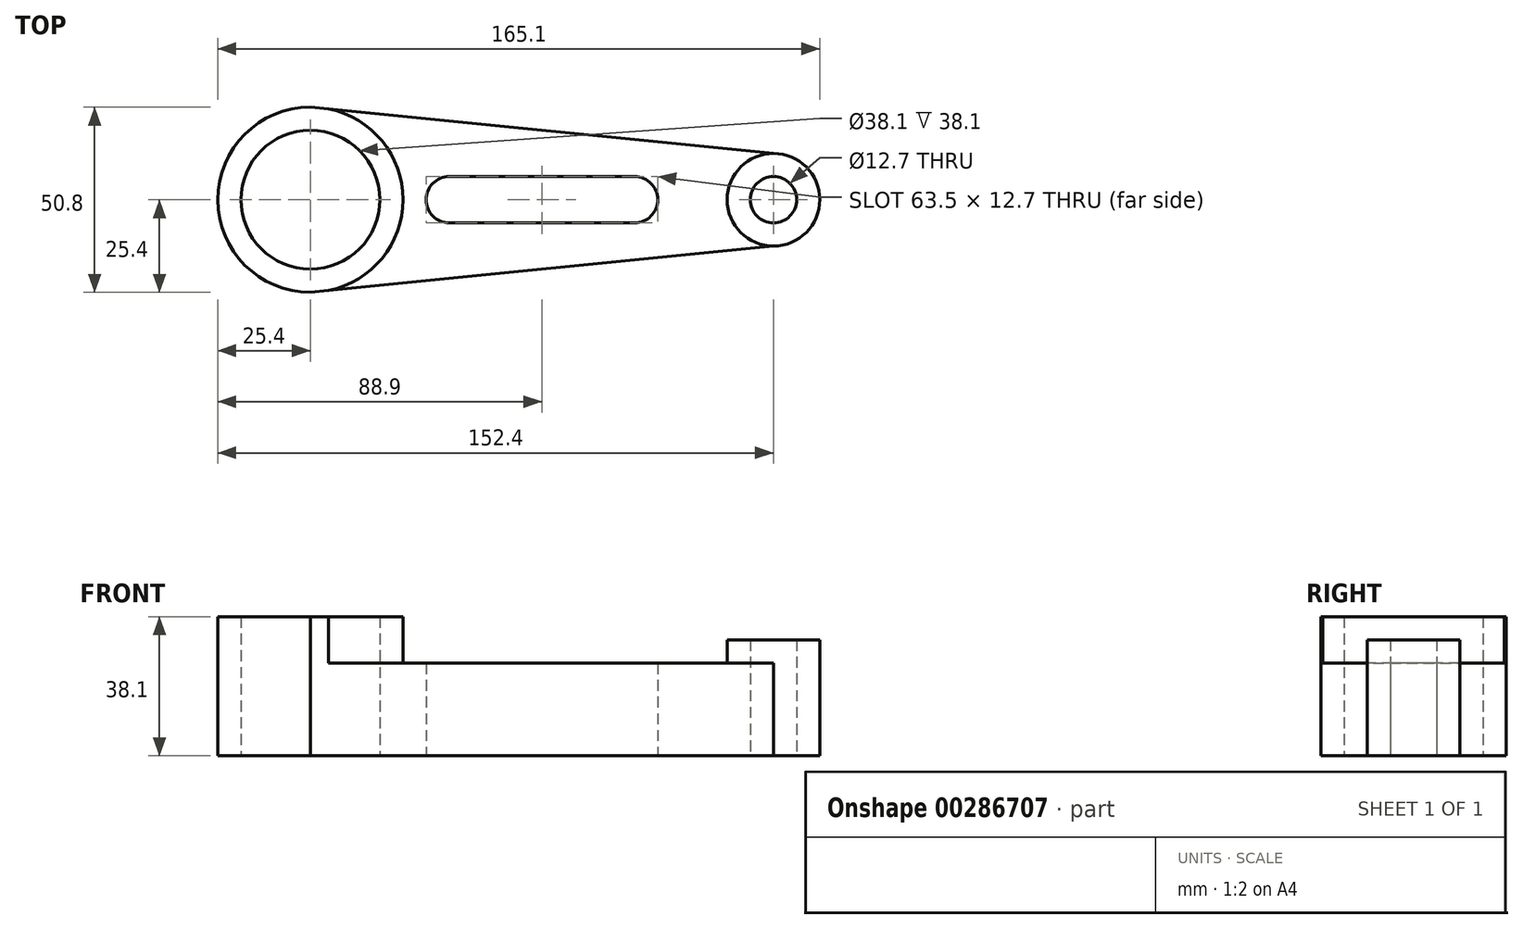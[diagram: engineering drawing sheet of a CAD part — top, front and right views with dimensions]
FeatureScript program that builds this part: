
annotation { "Feature Type Name" : "Feature", "Feature Type Description" : "" }
export const myFeature = defineFeature(function(context is Context, id is Id, definition is map)
    precondition{}
    {
        {
            var Q0;
            Q0=qCreatedBy(makeId("Top.planeOp"),FACE);
            var sketch = newSketch(context, id + "F0", { "sketchPlane" : qUnion([Q0])});
            skPoint(sketch, "E0", {"position": v(-25.4, 0) * mm});
            skPoint(sketch, "E1", {"position": v(25.4, 0) * mm});
            skCircle(sketch, "E2", {"center": v(-63.5, 0) * mm, "radius": 19.05 * mm});
            skCircle(sketch, "E3", {"center": v(-63.5, 0) * mm, "radius": 25.4 * mm});
            skCircle(sketch, "E4", {"center": v(63.5, 0) * mm, "radius": 12.7 * mm});
            skCircle(sketch, "E5", {"center": v(63.5, 0) * mm, "radius": 6.35 * mm});
            skArc(sketch, "E6", {"start": v(-25.4, 6.35) * mm, "mid": v(-31.75, 0) * mm, "end": v(-25.4, -6.35) * mm});
            skArc(sketch, "E7", {"start": v(25.4, -6.35) * mm, "mid": v(31.75, 0) * mm, "end": v(25.4, 6.35) * mm});
            skPoint(sketch, "E8", {"position": v(-25.4, -6.35) * mm});
            skPoint(sketch, "E9", {"position": v(25.4, 6.35) * mm});
            skPoint(sketch, "E10", {"position": v(25.4, -6.35) * mm});
            skPoint(sketch, "E11", {"position": v(-25.4, 6.35) * mm});
            skPoint(sketch, "E12", {"position": v(-63.5, 25.4) * mm});
            skPoint(sketch, "E13", {"position": v(-63.5, -25.4) * mm});
            skPoint(sketch, "E14", {"position": v(63.5, 12.7) * mm});
            skPoint(sketch, "E15", {"position": v(63.5, -12.7) * mm});
            skLineSegment(sketch, "E16", {"start": v(-63.5, 25.4) * mm, "end": v(63.5, 12.7) * mm});
            skLineSegment(sketch, "E17", {"start": v(-63.5, -25.4) * mm, "end": v(63.5, -12.7) * mm});
            skLineSegment(sketch, "E18", {"start": v(-25.4, 6.35) * mm, "end": v(25.4, 6.35) * mm});
            skLineSegment(sketch, "E19", {"start": v(25.4, -6.35) * mm, "end": v(-25.4, -6.35) * mm});
            skSolve(sketch);
        }
        {
            var Q0;
            {var subQ0=sQuery(id+"F0.wireOp",EDGE,"E16");var subQ1=sQuery(id+"F0.wireOp",EDGE,"E3");var subQ2=makeQuery(id+"F0.imprint","INTERSECT",VERTEX,{"disambiguationData":[OD(0.0)],"derivedFrom":[subQ1,subQ0]});Q0=makeQuery(id+"F0.imprint","IMPRINT",FACE,{"disambiguationData":[TD([[makeQuery(id+"F0.imprint","IMPRINT",EDGE,{"disambiguationData":[TD([[subQ2,1.0]])],"derivedFrom":subQ1}),1.0]])]});}
            var Q1;
            {var subQ0=sQuery(id+"F0.wireOp",EDGE,"E17");var subQ1=sQuery(id+"F0.wireOp",EDGE,"E3");var subQ2=makeQuery(id+"F0.imprint","INTERSECT",VERTEX,{"disambiguationData":[OD(0.0)],"derivedFrom":[subQ1,subQ0]});Q1=makeQuery(id+"F0.imprint","IMPRINT",FACE,{"disambiguationData":[TD([[makeQuery(id+"F0.imprint","IMPRINT",EDGE,{"disambiguationData":[TD([[subQ2,-1.0]])],"derivedFrom":subQ1}),1.0]])]});}
            var Q2;
            Q2=makeQuery(id+"F0.imprint","IMPRINT",FACE,{"disambiguationData":[TD([[makeQuery(id+"F0.imprint","IMPRINT",EDGE,{"derivedFrom":sQuery(id+"F0.wireOp",EDGE,"E6")}),-1.0]])]});
            extrude(context, id + "F1", {"entities" : qUnion([Q0, Q1, Q2]), "depth" : 25.4 * mm});
        }
        {
            var Q0;
            Q0=makeQuery(id+"F0.imprint","IMPRINT",FACE,{"disambiguationData":[TD([[makeQuery(id+"F0.imprint","IMPRINT",EDGE,{"derivedFrom":sQuery(id+"F0.wireOp",EDGE,"E2")}),-1.0]])]});
            extrude(context, id + "F2", {"entities" : qUnion([Q0]), "operationType" : NewBodyOperationType.ADD, "depth" : 38.1 * mm});
        }
        {
            var Q0;
            Q0=makeQuery(id+"F0.imprint","IMPRINT",FACE,{"disambiguationData":[TD([[makeQuery(id+"F0.imprint","IMPRINT",EDGE,{"derivedFrom":sQuery(id+"F0.wireOp",EDGE,"E5")}),-1.0]])]});
            extrude(context, id + "F3", {"entities" : qUnion([Q0]), "operationType" : NewBodyOperationType.ADD, "depth" : 31.75 * mm});
        }
    });
